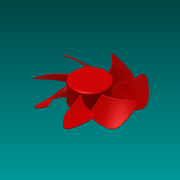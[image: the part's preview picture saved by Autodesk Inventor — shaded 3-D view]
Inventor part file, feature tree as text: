
AUTODESK INVENTOR PART (.ipt)
format: ipt  version: 2015 (Build 190159000, 159)  size: 1,250,304 bytes
history: native  units: mm
features: fillet x6, sketch x3, extrude x2, helix x1
ambient origin geometry x8: Origin, YZ Plane, XZ Plane, XY Plane, X Axis, Y Axis, Z Axis, Center Point
bodies: Solid1 (feature_tree)
feature tree (12):
  helix  "Coil1"  [1 undecoded]
  fillet  "Fillet1"  Radius=30.0mm
  extrude  "Extrusion1"  Depth=1.0mm
  fillet  "Fillet2"  Radius=70.0mm
  fillet  "Fillet3"  Radius=15.0mm
  fillet  "Fillet4"  Radius=4.0mm
  fillet  "Fillet5"  Radius=30.0mm
  fillet  "Fillet6"  Radius=2.0mm
  extrude  "Extrusion2"  Depth=10.0mm
  sketch  "Sketch1"  dims[d2=37.0mm d3=1.0mm d4=70.0mm d6=360.0deg d8=15.0mm]
  sketch  "Sketch2"  dims[d9=150.0mm d10=14.0mm d11=10.0mm d12=0.0mm d13=90.0deg d14=90.0deg d15=0.0mm d16=0.0mm d17=4.0mm d18=30.0mm d19=2.0mm d20=0.0mm]
  sketch  "Sketch3"  dims[d21=1.5mm d22=0.3mm d23=0.3mm d24=0.3mm d25=0.3mm d26=10.0mm d27=0.0mm]
note: 1 required parameter value undecoded (feature->parameter linkage not recoverable at this tier; creation-order binding heuristic only, values carry confidence <= 0.55)
